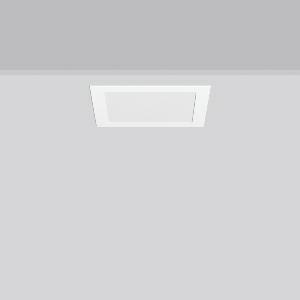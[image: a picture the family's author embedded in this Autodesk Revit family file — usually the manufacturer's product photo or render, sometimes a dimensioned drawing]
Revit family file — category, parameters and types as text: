
# Revit family: toledo_flat_square_e_672243_002_1_89_9464
name_source: partatom
category: Lighting Fixtures
units: mm (PartAtom-declared; Revit-internal decimal feet)

## family parameters
Cut with Voids When Loaded = No
Host = Face
Light Source = No
Part Type = Normal
Room Calculation Point = No
Round Connector Dimension = Use Diameter
Shared = No

## types (1)
- TOLEDO FLAT square E (1 x LED Modul 840, 1650 lm, 4000)
    Apparent Load = 19 VA
    CIE Flux Codes = 49 80 96 100 100
    Color Rendering = 80
    Color Temperature = 4000
    Default Elevation = 1800 mm
    Description = Series: TOLEDO FLAT square
Square recessed downlight. For escape route illumination. Housing: die-cast aluminium, powder-coated. Lightguide and diffuser made of non-yellowing plastic (PMMA). Diffuser opal matt plastic. Ceiling installation with spring system. Including separate LED converter with connecting cable 250 mm. Suitable for connection to central battery systems. With AC Control monitoring module for LUXIFAIR central battery units. External driver with simple plug-in locking system. 
Colour: white
Length: 225 mm
Width: 225 mm
Height: 3 mm
Cut-out length: 208 mm
Cut-out width: 208 mm
Recess height: 40 mm
Luminaire: recess height: 37-57 mm
Weight: 1.47 kg
Operating mode: maintained power mode
Lamp: LED
Socket: without socket
Colour temperature: 4000K
Colour rendering index (CRI): 80
System power: 19 W
Rated luminous flux: 1650 lm
Luminous flux, emergency: 1650 lm
System power, emergency: 19 W
Control gear: Regulated power supply
Protection class: I
Type of protection: IP 54
    Height = 0 mm  [stored 0 ft]
    Lamp = 1 x LED Modul 840
    Lamp Light Flux = 1650 lm
    Lamp count = 1
    Length = 225 mm
    Lifetime = 50000 h
    Luminous efficacy = 87 lm/W
    Manufacturer = RZB
    ModVariant = No
    Model = 672243.002.1.89
    Mounting Place = Ceiling
    Mounting Type = Recessed
    Number of Poles = 1
    OnlyDefault = Yes
    Power Factor = 1
    Product Name = TOLEDO FLAT square E
    Product group = Recessed downlights
    ProductGroupID = 402
    Protection Class = Protection class I
    Protection Degree = IP 40
    RLX_Detail_Level = 1
    RLX_Emergency_Light_Flux = 1650 lm
    RLX_Emergency_Type = 3
    RLX_Emergency_Type_DB = Yes
    RlxData = <blob elided: 11057 chars, md5=0c092ebf>
    Socket = socket
    Standby Power = 0 W
    System Light Flux = 1650 lm
    System Power = 19 W
    Type Comments = Product without accessories
    Type Image = 901487.002.jpg
    URL = http://relux.com
    VarID = ---
    Voltage = 230 V
    Voltage Range = 220-240 V
    Weight = 0.00 kg
    Width = 225 mm

note: [stored X ft] marks values corroborated as IEEE doubles in the binary element streams (Revit-internal decimal feet)

## geometry (parser evidence)
native form markers: Sweep x10
no freeform markers — native parametric forms only
